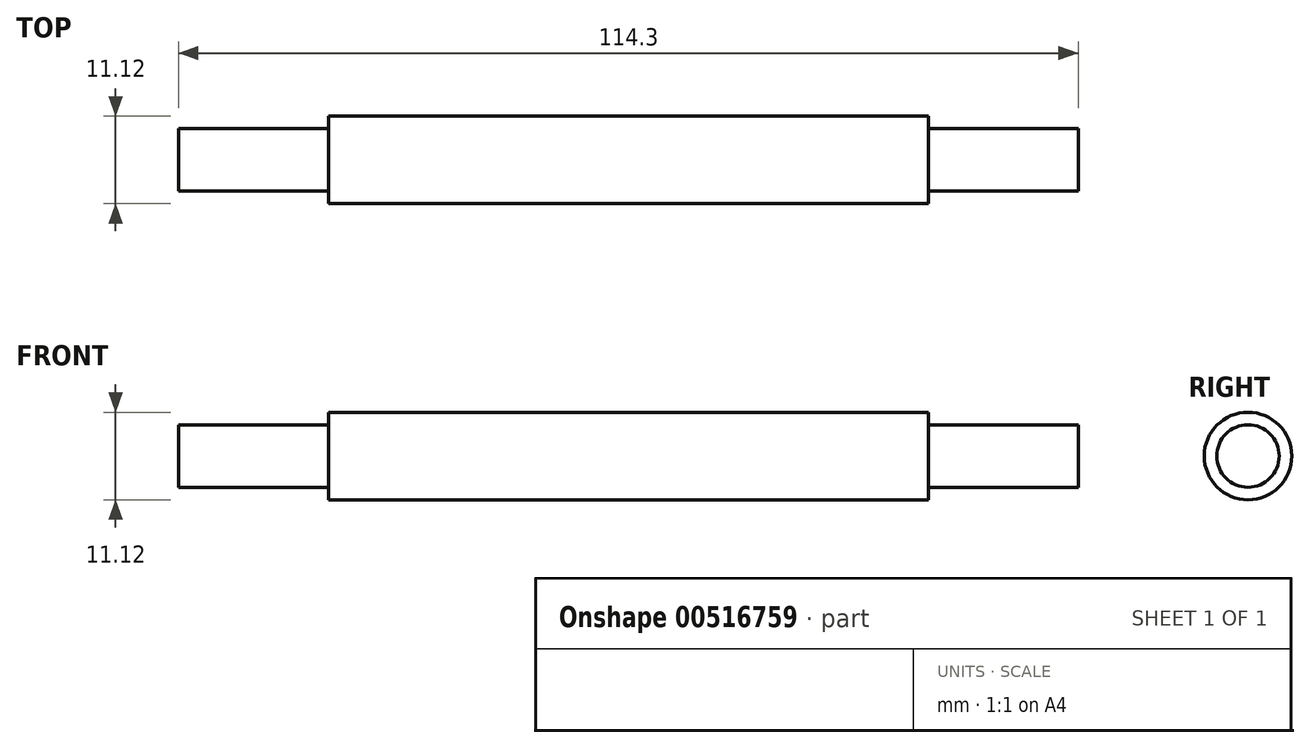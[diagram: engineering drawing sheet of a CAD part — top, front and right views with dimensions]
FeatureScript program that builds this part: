
annotation { "Feature Type Name" : "Feature", "Feature Type Description" : "" }
export const myFeature = defineFeature(function(context is Context, id is Id, definition is map)
    precondition{}
    {
        {
            var Q0;
            Q0=qCreatedBy(makeId("Right.planeOp"),FACE);
            var sketch = newSketch(context, id + "F0", { "sketchPlane" : qUnion([Q0])});
            skCircle(sketch, "E0", {"center": v(0, 0) * mm, "radius": 5.56 * mm});
            skSolve(sketch);
        }
        {
            var Q0;
            Q0=makeQuery(id+"F0.imprint","IMPRINT",FACE,{"disambiguationData":[TD([[makeQuery(id+"F0.imprint","IMPRINT",EDGE,{"derivedFrom":sQuery(id+"F0.wireOp",EDGE,"E0")}),1.0]])]});
            extrude(context, id + "F1", {"entities" : qUnion([Q0]), "depth" : 38.1 * mm, "offsetDistance" : 25.4 * mm});
        }
        {
            var Q0;
            Q0=makeQuery(id+"F1.opExtrude","CAP_FACE",FACE,{"disambiguationData":[OSD([sQuery(id+"F0.wireOp",EDGE,"E0")])],"isStart":false});
            var sketch = newSketch(context, id + "F2", { "sketchPlane" : qUnion([Q0])});
            skCircle(sketch, "E1", {"center": v(0, 0) * mm, "radius": 3.97 * mm});
            skSolve(sketch);
        }
        {
            var Q0;
            Q0=makeQuery(id+"F2.imprint","IMPRINT",FACE,{"disambiguationData":[TD([[makeQuery(id+"F2.imprint","IMPRINT",EDGE,{"derivedFrom":sQuery(id+"F2.wireOp",EDGE,"E1")}),1.0]])]});
            extrude(context, id + "F3", {"entities" : qUnion([Q0]), "operationType" : NewBodyOperationType.ADD, "depth" : 19.05 * mm, "offsetDistance" : 25.4 * mm});
        }
        {
            var Q0;
            Q0=makeQuery(id+"F1.opExtrude","SWEPT_BODY",BODY,{"disambiguationData":[OSD([sQuery(id+"F0.wireOp",EDGE,"E0")])]});
            var Q1;
            Q1=qCreatedBy(makeId("Right.planeOp"),FACE);
            mirror(context, id + "F4", {"operationType" : NewBodyOperationType.ADD, "entities" : qUnion([Q0]), "mirrorPlane" : qUnion([Q1])});
        }
    });
